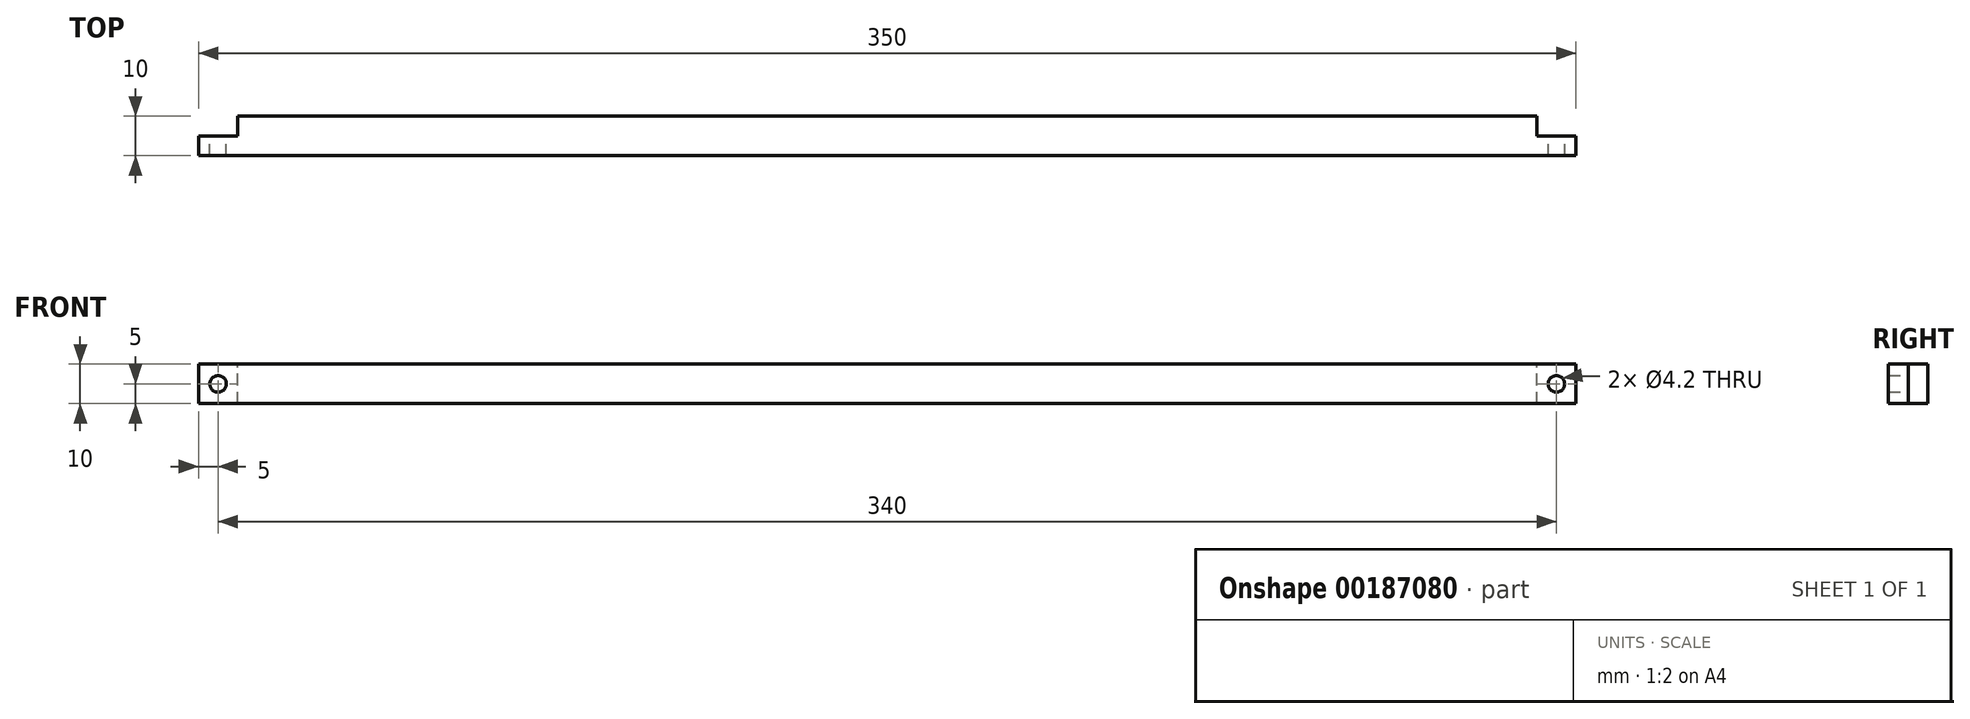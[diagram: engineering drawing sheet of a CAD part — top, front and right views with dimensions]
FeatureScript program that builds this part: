
annotation { "Feature Type Name" : "Feature", "Feature Type Description" : "" }
export const myFeature = defineFeature(function(context is Context, id is Id, definition is map)
    precondition{}
    {
        {
            var Q0;
            Q0=qCreatedBy(makeId("Right.planeOp"),FACE);
            var sketch = newSketch(context, id + "F0", { "sketchPlane" : qUnion([Q0])});
            skLineSegment(sketch, "E0", {"start": v(0, 0) * mm, "end": v(0, 165) * mm});
            skLineSegment(sketch, "E1", {"start": v(0, 165) * mm, "end": v(-5, 165) * mm});
            skLineSegment(sketch, "E2", {"start": v(-5, 165) * mm, "end": v(-5, 175) * mm});
            skLineSegment(sketch, "E3", {"start": v(-5, 175) * mm, "end": v(-10, 175) * mm});
            skLineSegment(sketch, "E4", {"start": v(-10, 175) * mm, "end": v(-10, 0) * mm});
            skLineSegment(sketch, "E5", {"start": v(-10, 0) * mm, "end": v(0, 0) * mm});
            skSolve(sketch);
        }
        {
            var Q0;
            Q0=qSketchRegion(id+"F0",true);
            extrude(context, id + "F1", {"entities" : qUnion([Q0]), "depth" : 10 * mm});
        }
        {
            var Q0;
            Q0=makeQuery(id+"F1.opExtrude","SWEPT_FACE",FACE,{"disambiguationData":[OSD([sQuery(id+"F0.wireOp",EDGE,"E2")])]});
            var sketch = newSketch(context, id + "F2", { "sketchPlane" : qUnion([Q0])});
            skCircle(sketch, "E6", {"center": v(-5, 170) * mm, "radius": 2.1 * mm});
            skPoint(sketch, "E6.centerSnap0", {"position": v(-5, 175) * mm});
            skPoint(sketch, "E6.centerSnap1", {"position": v(0, 170) * mm});
            skSolve(sketch);
        }
        {
            var Q0;
            Q0=qSketchRegion(id+"F2",true);
            extrude(context, id + "F3", {"entities" : qUnion([Q0]), "operationType" : NewBodyOperationType.REMOVE, "endBound" : BoundingType.THROUGH_ALL, "oppositeDirection" : true, "depth" : 4.5 * mm});
        }
        {
            var Q0;
            Q0=makeQuery(id+"F1.opExtrude","SWEPT_BODY",BODY,{"disambiguationData":[OSD([sQuery(id+"F0.wireOp",EDGE,"E0"),sQuery(id+"F0.wireOp",EDGE,"E1"),sQuery(id+"F0.wireOp",EDGE,"E2"),sQuery(id+"F0.wireOp",EDGE,"E3"),sQuery(id+"F0.wireOp",EDGE,"E4"),sQuery(id+"F0.wireOp",EDGE,"E5")])]});
            var Q1;
            Q1=qCreatedBy(makeId("Top.planeOp"),FACE);
            mirror(context, id + "F4", {"operationType" : NewBodyOperationType.ADD, "entities" : qUnion([Q0]), "mirrorPlane" : qUnion([Q1])});
        }
        {
            var Q0;
            Q0=makeQuery(id+"F1.opExtrude","SWEPT_BODY",BODY,{"disambiguationData":[OSD([sQuery(id+"F0.wireOp",EDGE,"E0"),sQuery(id+"F0.wireOp",EDGE,"E1"),sQuery(id+"F0.wireOp",EDGE,"E2"),sQuery(id+"F0.wireOp",EDGE,"E3"),sQuery(id+"F0.wireOp",EDGE,"E4"),sQuery(id+"F0.wireOp",EDGE,"E5")])]});
            var Q1;
            Q1=sQuery(id+"F0.wireOp",EDGE,"E5");
            var Q2;
            Q2=sQuery(id+"F0.wireOp",EDGE,"E5");
            transform(context, id + "F5", {"entities" : qUnion([Q0]), "transformType" : TransformType.ROTATION, "transformAxis" : qUnion([Q2]), "angle" : 90 * degree, "makeCopy" : false});
        }
    });
